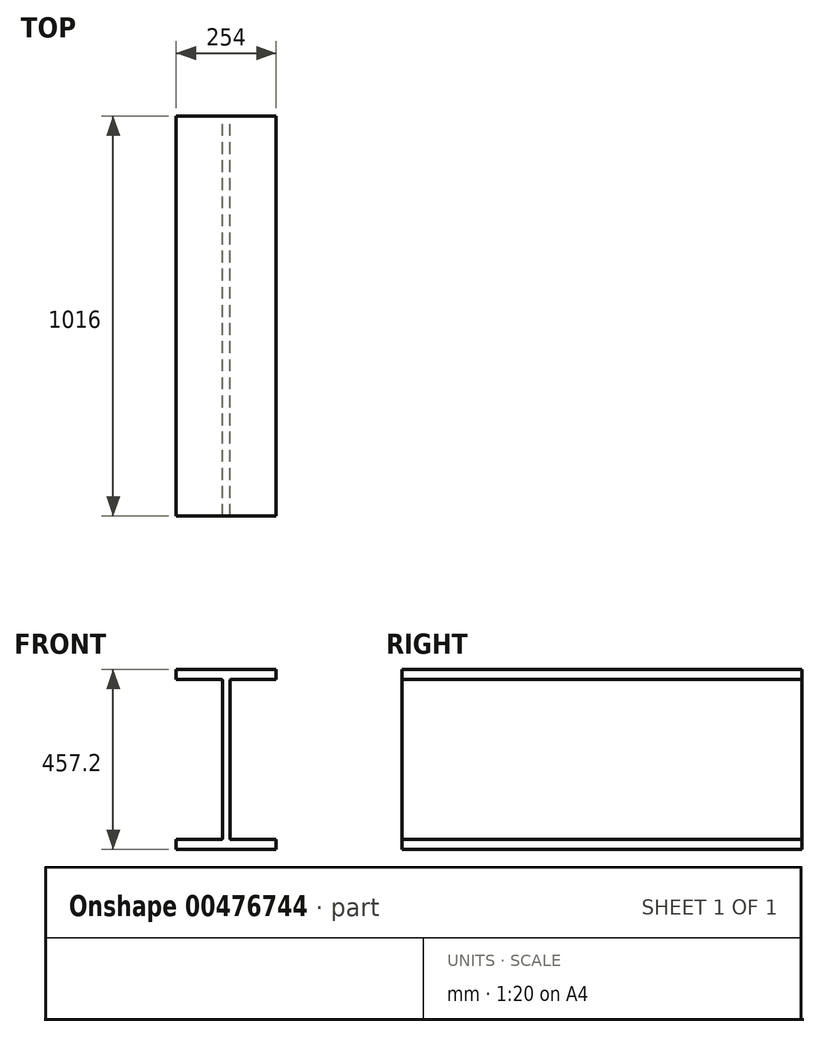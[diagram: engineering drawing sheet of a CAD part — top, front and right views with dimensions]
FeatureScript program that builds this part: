
annotation { "Feature Type Name" : "Feature", "Feature Type Description" : "" }
export const myFeature = defineFeature(function(context is Context, id is Id, definition is map)
    precondition{}
    {
        {
            var Q0;
            Q0=qCreatedBy(makeId("Front.planeOp"),FACE);
            var sketch = newSketch(context, id + "F0", { "sketchPlane" : qUnion([Q0])});
            skLineSegment(sketch, "E0", {"start": v(127, -203.2) * mm, "end": v(12.06, -203.2) * mm});
            skLineSegment(sketch, "E1", {"start": v(9.52, -200.66) * mm, "end": v(9.52, 200.66) * mm});
            skLineSegment(sketch, "E2", {"start": v(12.06, 203.2) * mm, "end": v(127, 203.2) * mm});
            skLineSegment(sketch, "E3", {"start": v(-127, 203.2) * mm, "end": v(-12.06, 203.2) * mm});
            skLineSegment(sketch, "E4", {"start": v(-9.53, 200.66) * mm, "end": v(-9.53, -200.66) * mm});
            skLineSegment(sketch, "E5", {"start": v(-12.06, -203.2) * mm, "end": v(-127, -203.2) * mm});
            skLineSegment(sketch, "E6", {"start": v(0, 0) * mm, "end": v(-9.52, 0) * mm, "construction": true});
            skLineSegment(sketch, "E7", {"start": v(0, 0) * mm, "end": v(9.52, 0) * mm, "construction": true});
            skLineSegment(sketch, "E8", {"start": v(0, 0) * mm, "end": v(0, 228.6) * mm, "construction": true});
            skLineSegment(sketch, "E9", {"start": v(0, 0) * mm, "end": v(0, -228.6) * mm, "construction": true});
            skPoint(sketch, "E10.visualSharp", {"position": v(-9.53, 203.2) * mm});
            skArc(sketch, "E10.filletArc", {"start": v(-9.52, 200.66) * mm, "mid": v(-10.27, 202.46) * mm, "end": v(-12.06, 203.2) * mm});
            skPoint(sketch, "E11.visualSharp", {"position": v(9.53, 203.2) * mm});
            skArc(sketch, "E11.filletArc", {"start": v(12.06, 203.2) * mm, "mid": v(10.27, 202.46) * mm, "end": v(9.52, 200.66) * mm});
            skPoint(sketch, "E12.visualSharp", {"position": v(9.53, -203.2) * mm});
            skArc(sketch, "E12.filletArc", {"start": v(9.52, -200.66) * mm, "mid": v(10.27, -202.46) * mm, "end": v(12.06, -203.2) * mm});
            skPoint(sketch, "E13.visualSharp", {"position": v(-9.53, -203.2) * mm});
            skArc(sketch, "E13.filletArc", {"start": v(-12.06, -203.2) * mm, "mid": v(-10.27, -202.46) * mm, "end": v(-9.52, -200.66) * mm});
            skPoint(sketch, "E14.visualSharp", {"position": v(-127, 228.6) * mm});
            skPoint(sketch, "E15.visualSharp", {"position": v(127, 228.6) * mm});
            skPoint(sketch, "E16.visualSharp", {"position": v(127, 203.2) * mm});
            skPoint(sketch, "E17.visualSharp", {"position": v(127, -228.6) * mm});
            skPoint(sketch, "E18.visualSharp", {"position": v(-127, -203.2) * mm});
            skPoint(sketch, "E19.visualSharp", {"position": v(-127, -228.6) * mm});
            skLineSegment(sketch, "E20", {"start": v(127, -203.2) * mm, "end": v(127, -228.6) * mm});
            skLineSegment(sketch, "E21", {"start": v(-127, -203.2) * mm, "end": v(-127, -228.6) * mm});
            skLineSegment(sketch, "E22", {"start": v(-127, 228.6) * mm, "end": v(-127, 203.2) * mm});
            skLineSegment(sketch, "E23", {"start": v(127, 228.6) * mm, "end": v(127, 203.2) * mm});
            skLineSegment(sketch, "E24", {"start": v(-127, 228.6) * mm, "end": v(127, 228.6) * mm});
            skLineSegment(sketch, "E25", {"start": v(-127, -228.6) * mm, "end": v(127, -228.6) * mm});
            skSolve(sketch);
        }
        {
            var Q0;
            Q0=makeQuery(id+"F0.imprint","IMPRINT",FACE,{"disambiguationData":[TD([[makeQuery(id+"F0.imprint","IMPRINT",EDGE,{"derivedFrom":sQuery(id+"F0.wireOp",EDGE,"E0")}),1.0]])]});
            extrude(context, id + "F1", {"entities" : qUnion([Q0]), "endBound" : BoundingType.SYMMETRIC, "depth" : 1016 * mm});
        }
    });
